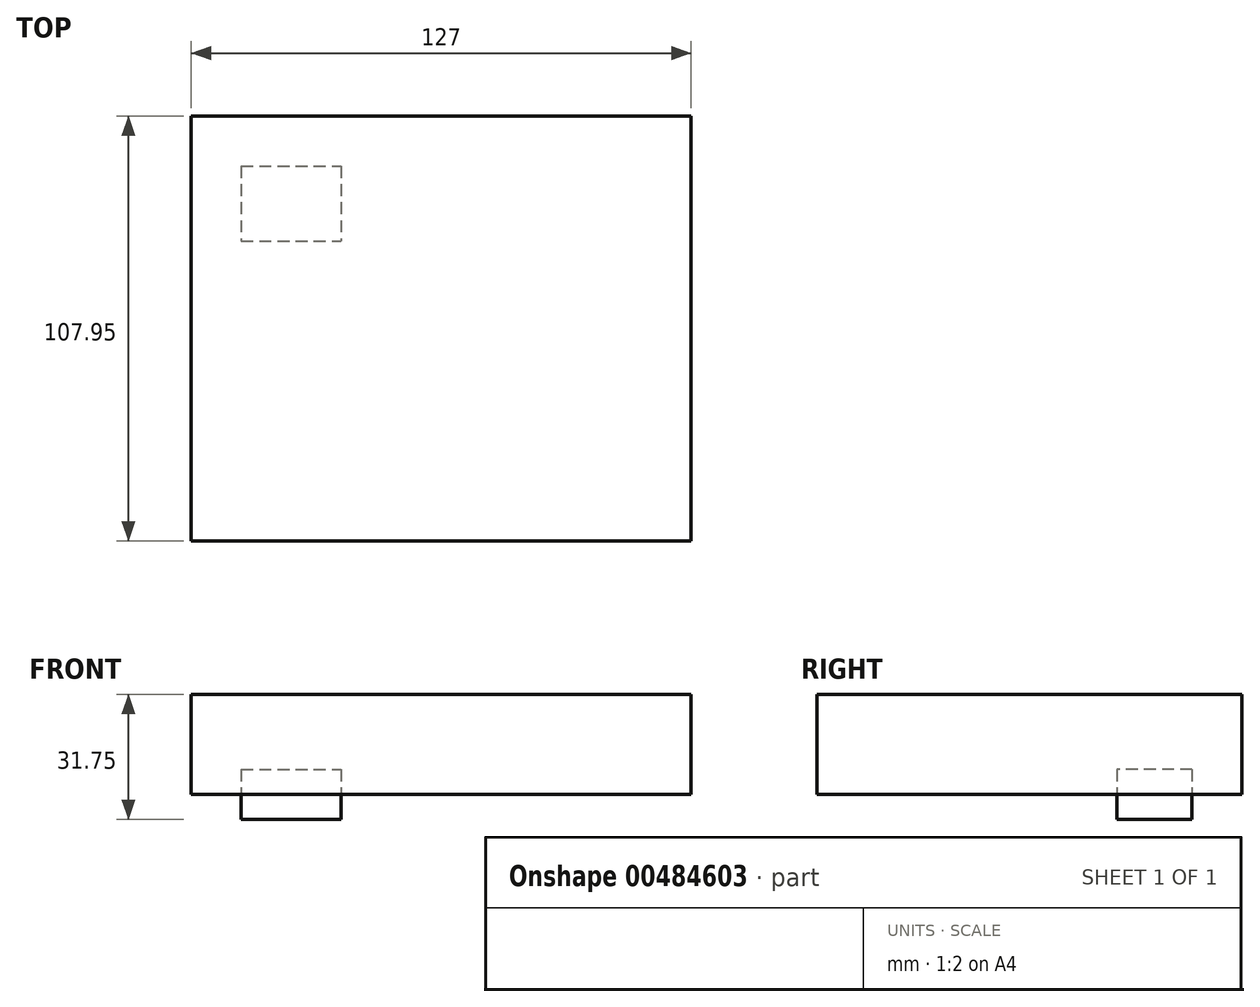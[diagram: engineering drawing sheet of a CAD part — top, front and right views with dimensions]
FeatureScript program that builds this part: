
annotation { "Feature Type Name" : "Feature", "Feature Type Description" : "" }
export const myFeature = defineFeature(function(context is Context, id is Id, definition is map)
    precondition{}
    {
        {
            var Q0;
            Q0=qCreatedBy(makeId("Top.planeOp"),FACE);
            var sketch = newSketch(context, id + "F0", { "sketchPlane" : qUnion([Q0])});
            skLineSegment(sketch, "E0.bottom", {"start": v(-64.32, 51.48) * mm, "end": v(62.68, 51.48) * mm});
            skLineSegment(sketch, "E0.top", {"start": v(-64.32, -56.47) * mm, "end": v(62.68, -56.47) * mm});
            skLineSegment(sketch, "E0.left", {"start": v(-64.32, 51.48) * mm, "end": v(-64.32, -56.47) * mm});
            skLineSegment(sketch, "E0.right", {"start": v(62.68, 51.48) * mm, "end": v(62.68, -56.47) * mm});
            skSolve(sketch);
        }
        {
            var Q0;
            Q0=makeQuery(id+"F0.imprint","IMPRINT",FACE,{"disambiguationData":[TD([[makeQuery(id+"F0.imprint","IMPRINT",EDGE,{"derivedFrom":sQuery(id+"F0.wireOp",EDGE,"E0.bottom")}),-1.0]])]});
            extrude(context, id + "F1", {"entities" : qUnion([Q0]), "depth" : 25.4 * mm});
        }
        {
            var Q0;
            Q0=qCreatedBy(makeId("Top.planeOp"),FACE);
            var sketch = newSketch(context, id + "F2", { "sketchPlane" : qUnion([Q0])});
            skLineSegment(sketch, "E1.bottom", {"start": v(-51.62, 38.78) * mm, "end": v(-26.22, 38.78) * mm});
            skLineSegment(sketch, "E1.top", {"start": v(-51.62, 19.73) * mm, "end": v(-26.22, 19.73) * mm});
            skLineSegment(sketch, "E1.left", {"start": v(-51.62, 38.78) * mm, "end": v(-51.62, 19.73) * mm});
            skLineSegment(sketch, "E1.right", {"start": v(-26.22, 38.78) * mm, "end": v(-26.22, 19.73) * mm});
            skSolve(sketch);
        }
        {
            var Q0;
            Q0 = qSketchRegion(id + "F2", true);
            extrude(context, id + "F3", {"entities" : qUnion([Q0]), "endBound" : BoundingType.SYMMETRIC, "depth" : 12.7 * mm});
        }
    });
